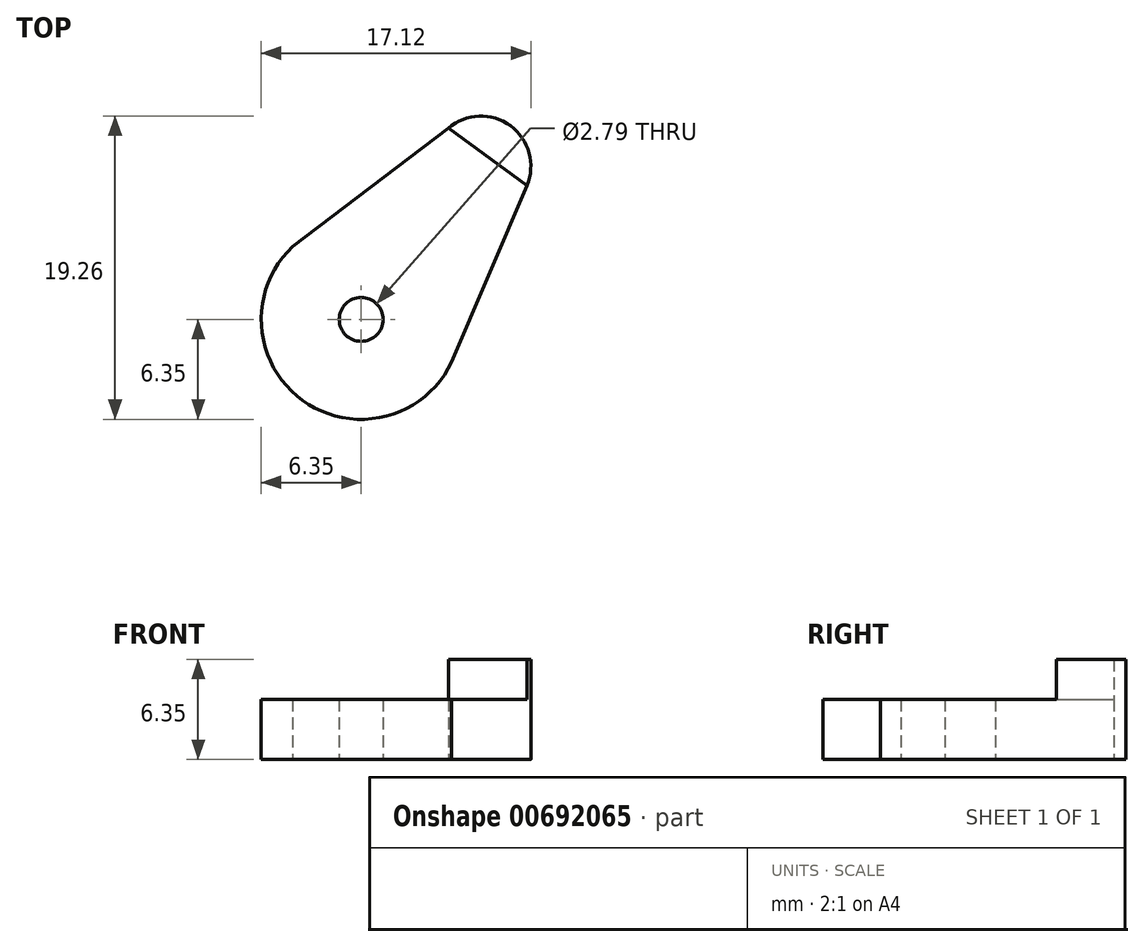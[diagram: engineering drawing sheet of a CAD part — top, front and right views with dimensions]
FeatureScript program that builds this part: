
annotation { "Feature Type Name" : "Feature", "Feature Type Description" : "" }
export const myFeature = defineFeature(function(context is Context, id is Id, definition is map)
    precondition{}
    {
        {
            var Q0;
            Q0=qCreatedBy(makeId("Top.planeOp"),FACE);
            var sketch = newSketch(context, id + "F0", { "sketchPlane" : qUnion([Q0])});
            skArc(sketch, "E0", {"start": v(-3.3, 5.43) * mm, "mid": v(-4.07, -4.87) * mm, "end": v(5.93, -2.28) * mm});
            skArc(sketch, "E1", {"start": v(10.52, 8.5) * mm, "mid": v(9.48, 12.3) * mm, "end": v(5.53, 12.15) * mm});
            skLineSegment(sketch, "E2", {"start": v(-4.35, 4.62) * mm, "end": v(5.53, 12.15) * mm});
            skLineSegment(sketch, "E3", {"start": v(5.75, -2.7) * mm, "end": v(10.52, 8.5) * mm});
            skCircle(sketch, "E4", {"center": v(0, 0) * mm, "radius": 1.4 * mm});
            skSolve(sketch);
        }
        {
            var Q0;
            {var subQ3=sQuery(id+"F0.wireOp",EDGE,"E1");Q0=makeQuery(id+"F0.imprint","IMPRINT",FACE,{"disambiguationData":[TD([[makeQuery(id+"F0.imprint","IMPRINT",EDGE,{"derivedFrom":subQ3}),1.0]])]});}
            extrude(context, id + "F1", {"entities" : qUnion([Q0]), "depth" : 3.8 * mm, "offsetDistance" : 25.4 * mm});
        }
        {
            var Q0;
            Q0=makeQuery(id+"F1.opExtrude","CAP_FACE",FACE,{"disambiguationData":[OSD([sQuery(id+"F0.wireOp",EDGE,"E0"),sQuery(id+"F0.wireOp",EDGE,"E1"),sQuery(id+"F0.wireOp",EDGE,"E2"),sQuery(id+"F0.wireOp",EDGE,"E3"),sQuery(id+"F0.wireOp",EDGE,"E4")])],"isStart":false});
            var sketch = newSketch(context, id + "F2", { "sketchPlane" : qUnion([Q0])});
            skLineSegment(sketch, "E5", {"start": v(10.52, 8.5) * mm, "end": v(5.53, 12.15) * mm});
            skSolve(sketch);
        }
        {
            var Q0;
            Q0=makeQuery(id+"F2.imprint","IMPRINT",FACE,{"disambiguationData":[TD([[makeQuery(id+"F2.imprint","IMPRINT",EDGE,{"derivedFrom":sQuery(id+"F2.wireOp",EDGE,"E5")}),-1.0]])]});
            extrude(context, id + "F3", {"entities" : qUnion([Q0]), "operationType" : NewBodyOperationType.ADD, "depth" : 2.54 * mm, "offsetDistance" : 25.4 * mm});
        }
    });
